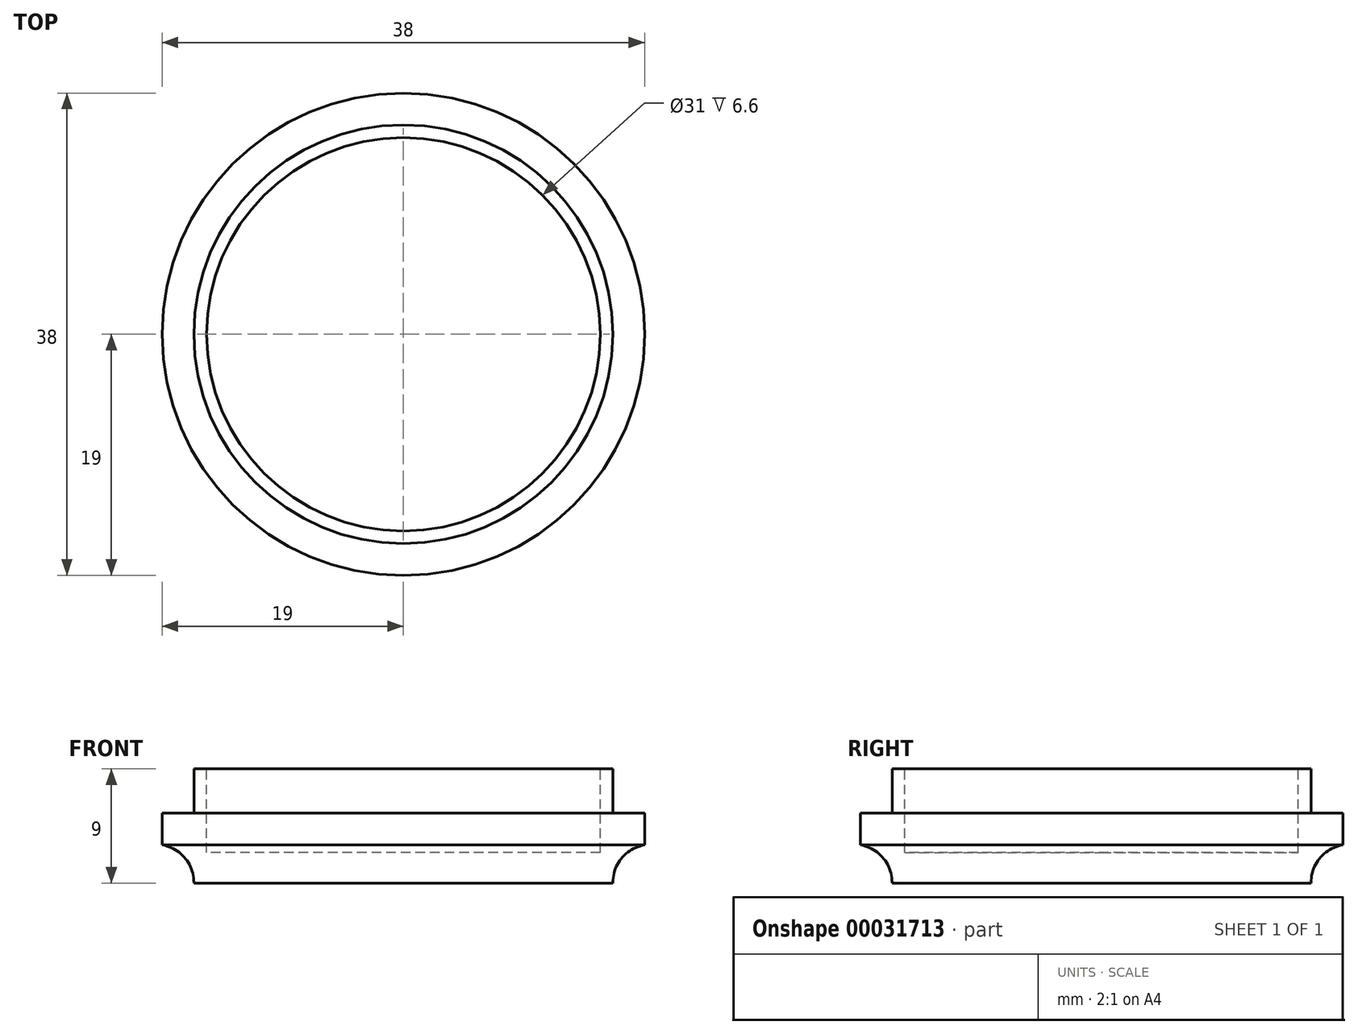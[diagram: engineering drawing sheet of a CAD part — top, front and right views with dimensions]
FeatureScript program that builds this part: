
annotation { "Feature Type Name" : "Feature", "Feature Type Description" : "" }
export const myFeature = defineFeature(function(context is Context, id is Id, definition is map)
    precondition{}
    {
        {
            var Q0;
            Q0=qCreatedBy(makeId("Top.planeOp"),FACE);
            var sketch = newSketch(context, id + "F0", { "sketchPlane" : qUnion([Q0])});
            skCircle(sketch, "E0", {"center": v(0, 0) * mm, "radius": 16.5 * mm});
            skSolve(sketch);
        }
        {
            var Q0;
            Q0=makeQuery(id+"F0.imprint","IMPRINT",FACE,{"disambiguationData":[TD([[makeQuery(id+"F0.imprint","IMPRINT",EDGE,{"derivedFrom":sQuery(id+"F0.wireOp",EDGE,"E0")}),1.0]])]});
            extrude(context, id + "F1", {"entities" : qUnion([Q0]), "depth" : 9 * mm});
        }
        {
            var Q0;
            Q0=makeQuery(id+"F1.opExtrude","CAP_FACE",FACE,{"disambiguationData":[OSD([sQuery(id+"F0.wireOp",EDGE,"E0")])],"isStart":false});
            var sketch = newSketch(context, id + "F2", { "sketchPlane" : qUnion([Q0])});
            skCircle(sketch, "E1", {"center": v(0, 0) * mm, "radius": 15.5 * mm});
            skSolve(sketch);
        }
        {
            var Q0;
            Q0=makeQuery(id+"F1.opExtrude","CAP_FACE",FACE,{"disambiguationData":[OSD([sQuery(id+"F0.wireOp",EDGE,"E0")])],"isStart":false});
            cPlane(context, id + "F3", {"entities" : qUnion([Q0]), "cplaneType" : CPlaneType.OFFSET, "offset" : 3.5 * mm, "oppositeDirection" : true, "width" : 150 * mm, "height" : 150 * mm});
        }
        {
            var Q0;
            Q0=qCreatedBy(id+"F3.planeOp",FACE);
            var sketch = newSketch(context, id + "F4", { "sketchPlane" : qUnion([Q0])});
            skCircle(sketch, "E2", {"center": v(0, 0) * mm, "radius": 19 * mm});
            skSolve(sketch);
        }
        {
            var Q0;
            Q0 = qSketchRegion(id + "F4", true);
            extrude(context, id + "F5", {"entities" : qUnion([Q0]), "operationType" : NewBodyOperationType.ADD, "oppositeDirection" : true, "depth" : 2.5 * mm});
        }
        {
            var Q0;
            Q0 = qSketchRegion(id + "F2", true);
            extrude(context, id + "F6", {"entities" : qUnion([Q0]), "operationType" : NewBodyOperationType.REMOVE, "oppositeDirection" : true, "depth" : 6.6 * mm});
        }
        {
            var Q0;
            Q0=makeQuery(id+"F5.boolean.opBoolean","INTERSECT",EDGE,{"derivedFrom":[makeQuery(id+"F1.opExtrude","SWEPT_FACE",FACE,{"disambiguationData":[OSD([sQuery(id+"F0.wireOp",EDGE,"E0")])]}),makeQuery(id+"F5.opExtrude","CAP_FACE",FACE,{"disambiguationData":[OSD([sQuery(id+"F4.wireOp",EDGE,"E2")])],"isStart":false})]});
            fillet(context, id + "F7", {"entities" : qUnion([Q0]), "radius" : 3 * mm, "tangentPropagation" : true, "allowEdgeOverflow" : false});
        }
    });
